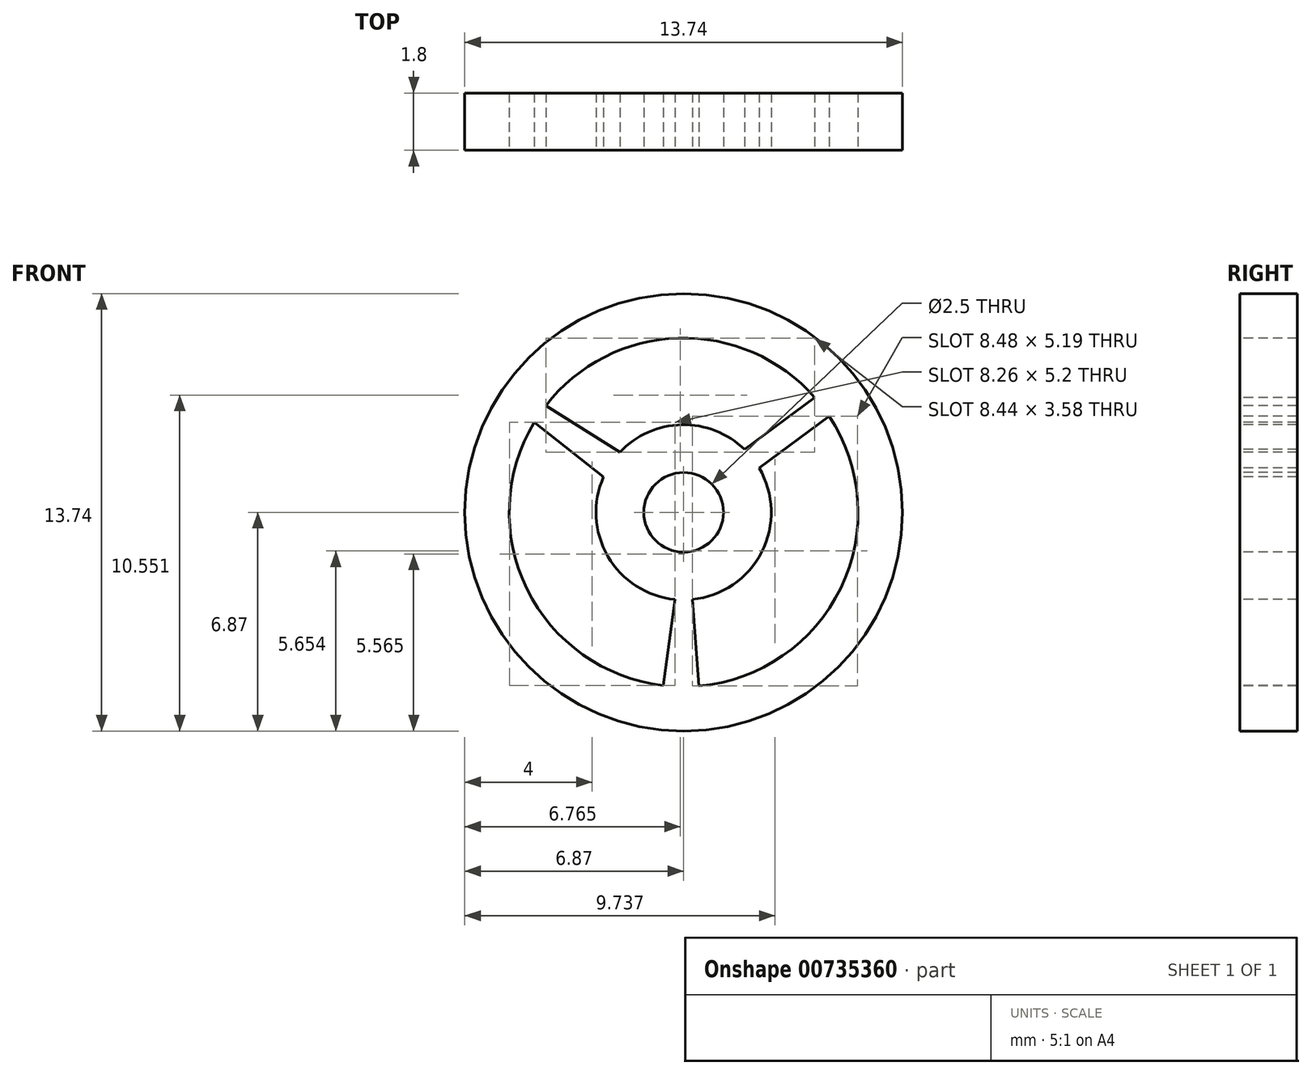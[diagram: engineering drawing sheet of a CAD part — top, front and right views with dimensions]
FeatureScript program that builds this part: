
annotation { "Feature Type Name" : "Feature", "Feature Type Description" : "" }
export const myFeature = defineFeature(function(context is Context, id is Id, definition is map)
    precondition{}
    {
        {
            var Q0;
            Q0=qCreatedBy(makeId("Front.planeOp"),FACE);
            var sketch = newSketch(context, id + "F0", { "sketchPlane" : qUnion([Q0])});
            skCircle(sketch, "E0", {"center": v(0, 0) * mm, "radius": 5.47 * mm});
            skCircle(sketch, "E1", {"center": v(0, 0) * mm, "radius": 2.75 * mm});
            skCircle(sketch, "E2", {"center": v(0, 0) * mm, "radius": 1.25 * mm});
            skLineSegment(sketch, "E3", {"start": v(1.91, 1.98) * mm, "end": v(4.12, 3.6) * mm});
            skLineSegment(sketch, "E4", {"start": v(2.37, 1.39) * mm, "end": v(4.57, 3.02) * mm});
            skLineSegment(sketch, "E5", {"start": v(-2, 1.89) * mm, "end": v(-4.33, 3.35) * mm});
            skLineSegment(sketch, "E6", {"start": v(-2.51, 1.12) * mm, "end": v(-4.69, 2.83) * mm});
            skLineSegment(sketch, "E7", {"start": v(0.27, -2.74) * mm, "end": v(0.48, -5.45) * mm});
            skLineSegment(sketch, "E8", {"start": v(-0.27, -2.74) * mm, "end": v(-0.64, -5.44) * mm});
            skCircle(sketch, "E9", {"center": v(0, 0) * mm, "radius": 6.87 * mm});
            skSolve(sketch);
        }
        {
            var Q0;
            Q0=makeQuery(id+"F0.imprint","IMPRINT",FACE,{"disambiguationData":[TD([[makeQuery(id+"F0.imprint","IMPRINT",EDGE,{"derivedFrom":sQuery(id+"F0.wireOp",EDGE,"E9")}),1.0]])]});
            var Q1;
            Q1=makeQuery(id+"F0.imprint","IMPRINT",FACE,{"disambiguationData":[TD([[makeQuery(id+"F0.imprint","IMPRINT",EDGE,{"derivedFrom":sQuery(id+"F0.wireOp",EDGE,"E2")}),-1.0]])]});
            var Q2;
            {var subQ0=sQuery(id+"F0.wireOp",EDGE,"E3");Q2=makeQuery(id+"F0.imprint","IMPRINT",FACE,{"disambiguationData":[TD([[makeQuery(id+"F0.imprint","IMPRINT",EDGE,{"derivedFrom":subQ0}),-1.0]])]});}
            var Q3;
            {var subQ0=sQuery(id+"F0.wireOp",EDGE,"E7");Q3=makeQuery(id+"F0.imprint","IMPRINT",FACE,{"disambiguationData":[TD([[makeQuery(id+"F0.imprint","IMPRINT",EDGE,{"derivedFrom":subQ0}),-1.0]])]});}
            var Q4;
            {var subQ0=sQuery(id+"F0.wireOp",EDGE,"E5");Q4=makeQuery(id+"F0.imprint","IMPRINT",FACE,{"disambiguationData":[TD([[makeQuery(id+"F0.imprint","IMPRINT",EDGE,{"derivedFrom":subQ0}),1.0]])]});}
            extrude(context, id + "F1", {"entities" : qUnion([Q0, Q1, Q2, Q3, Q4]), "oppositeDirection" : true, "depth" : 1.8 * mm, "offsetDistance" : 25 * mm});
        }
    });
